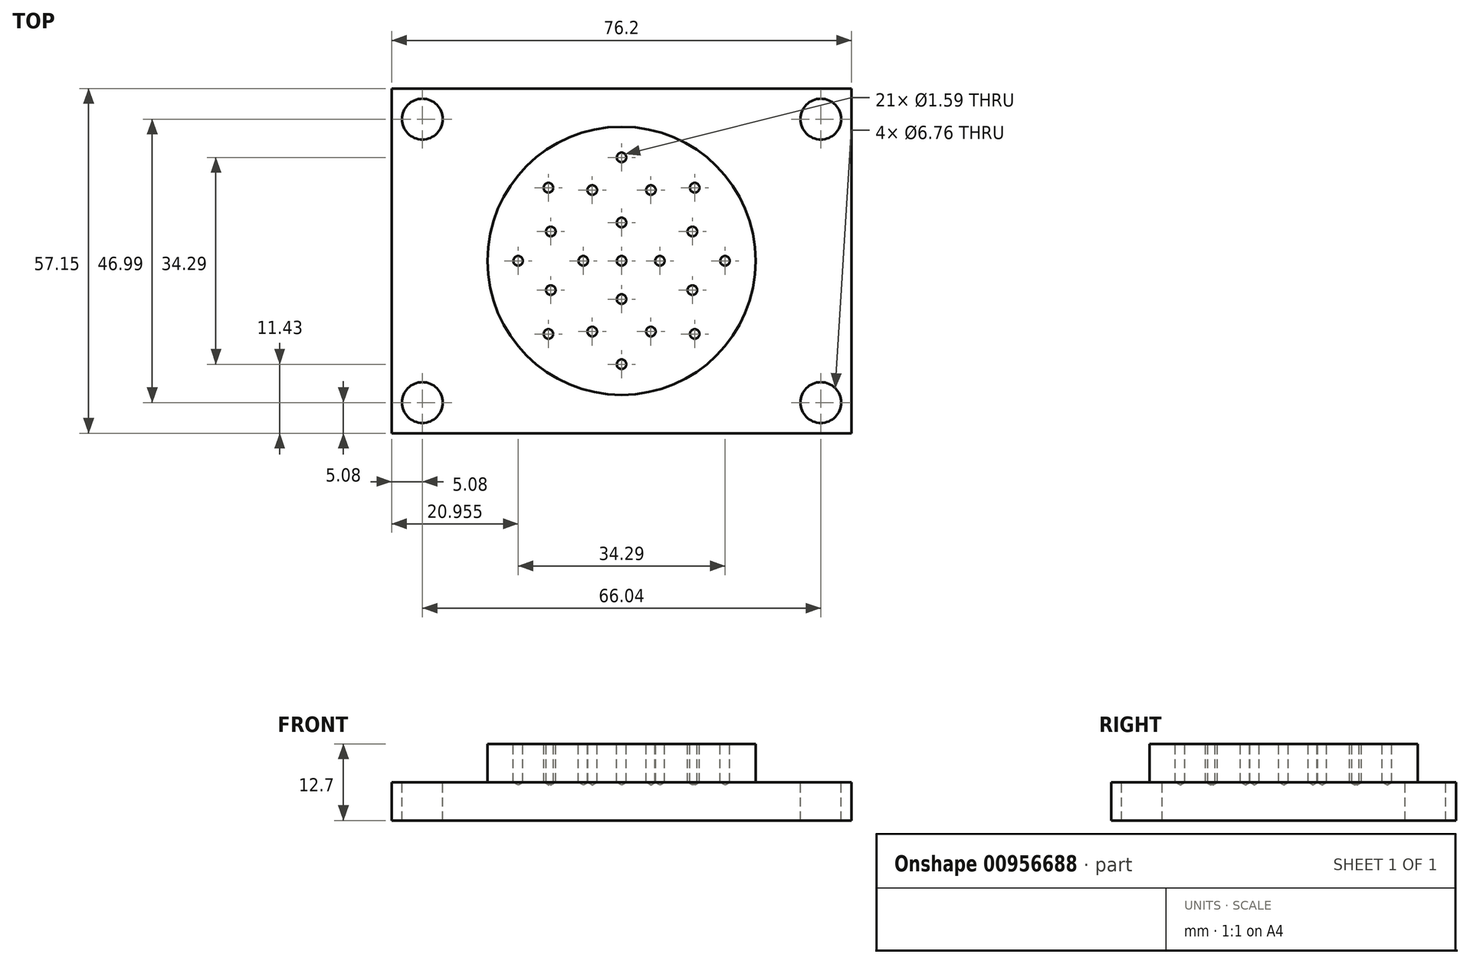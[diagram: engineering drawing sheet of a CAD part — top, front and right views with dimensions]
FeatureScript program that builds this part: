
annotation { "Feature Type Name" : "Feature", "Feature Type Description" : "" }
export const myFeature = defineFeature(function(context is Context, id is Id, definition is map)
    precondition{}
    {
        {
            var Q0;
            Q0=qCreatedBy(makeId("Top.planeOp"),FACE);
            var sketch = newSketch(context, id + "F0", { "sketchPlane" : qUnion([Q0])});
            skLineSegment(sketch, "E0.bottom", {"start": v(0, 0) * mm, "end": v(76.2, 0) * mm});
            skLineSegment(sketch, "E0.top", {"start": v(0, 57.15) * mm, "end": v(76.2, 57.15) * mm});
            skLineSegment(sketch, "E0.left", {"start": v(0, 0) * mm, "end": v(0, 57.15) * mm});
            skLineSegment(sketch, "E0.right", {"start": v(76.2, 0) * mm, "end": v(76.2, 57.15) * mm});
            skSolve(sketch);
        }
        {
            var Q0;
            Q0=makeQuery(id+"F0.imprint","IMPRINT",FACE,{"disambiguationData":[TD([[makeQuery(id+"F0.imprint","IMPRINT",EDGE,{"derivedFrom":sQuery(id+"F0.wireOp",EDGE,"E0.bottom")}),1.0]])]});
            extrude(context, id + "F1", {"entities" : qUnion([Q0]), "depth" : 6.35 * mm, "offsetDistance" : 25.4 * mm});
        }
        {
            var Q0;
            Q0=makeQuery(id+"F1.opExtrude","CAP_FACE",FACE,{"disambiguationData":[OSD([sQuery(id+"F0.wireOp",EDGE,"E0.bottom"),sQuery(id+"F0.wireOp",EDGE,"E0.top"),sQuery(id+"F0.wireOp",EDGE,"E0.left"),sQuery(id+"F0.wireOp",EDGE,"E0.right")])],"isStart":false});
            var sketch = newSketch(context, id + "F2", { "sketchPlane" : qUnion([Q0])});
            skCircle(sketch, "E1", {"center": v(38.1, 28.57) * mm, "radius": 22.23 * mm});
            skLineSegment(sketch, "E2", {"start": v(0, 0) * mm, "end": v(76.2, 57.15) * mm, "construction": true});
            skSolve(sketch);
        }
        {
            var Q0;
            Q0=makeQuery(id+"F2.imprint","IMPRINT",FACE,{"disambiguationData":[TD([[makeQuery(id+"F2.imprint","IMPRINT",EDGE,{"derivedFrom":sQuery(id+"F2.wireOp",EDGE,"E1")}),1.0]])]});
            extrude(context, id + "F3", {"entities" : qUnion([Q0]), "operationType" : NewBodyOperationType.ADD, "depth" : 6.35 * mm, "offsetDistance" : 25.4 * mm});
        }
        {
            var Q0;
            Q0=makeQuery(id+"F1.opExtrude","CAP_FACE",FACE,{"disambiguationData":[OSD([sQuery(id+"F0.wireOp",EDGE,"E0.bottom"),sQuery(id+"F0.wireOp",EDGE,"E0.top"),sQuery(id+"F0.wireOp",EDGE,"E0.left"),sQuery(id+"F0.wireOp",EDGE,"E0.right")])],"isStart":false});
            var sketch = newSketch(context, id + "F4", { "sketchPlane" : qUnion([Q0])});
            skPoint(sketch, "E3", {"position": v(5.08, 5.08) * mm});
            skLineSegment(sketch, "E4.bottom", {"start": v(5.08, 5.08) * mm, "end": v(71.12, 5.08) * mm, "construction": true});
            skLineSegment(sketch, "E4.top", {"start": v(5.08, 52.07) * mm, "end": v(71.12, 52.07) * mm, "construction": true});
            skLineSegment(sketch, "E4.left", {"start": v(5.08, 5.08) * mm, "end": v(5.08, 52.07) * mm, "construction": true});
            skLineSegment(sketch, "E4.right", {"start": v(71.12, 5.08) * mm, "end": v(71.12, 52.07) * mm, "construction": true});
            skSolve(sketch);
        }
        {
            var Q0;
            Q0=sQuery(id+"F4.wireOp",VERTEX,"E3");
            var Q1;
            Q1=sQuery(id+"F4.wireOp",VERTEX,"E4.top.start");
            var Q2;
            Q2=sQuery(id+"F4.wireOp",VERTEX,"E4.top.end");
            var Q3;
            Q3=sQuery(id+"F4.wireOp",VERTEX,"E4.bottom.end");
            var Q4;
            Q4=makeQuery(id+"F1.opExtrude","SWEPT_BODY",BODY,{"disambiguationData":[OSD([sQuery(id+"F0.wireOp",EDGE,"E0.bottom"),sQuery(id+"F0.wireOp",EDGE,"E0.top"),sQuery(id+"F0.wireOp",EDGE,"E0.left"),sQuery(id+"F0.wireOp",EDGE,"E0.right")])]});
            hole(context, id + "F5", {"style" : HoleStyle.SIMPLE, "endStyle" : HoleEndStyle.THROUGH, "standardTappedOrClearance" : lookupTablePath({ "fit" : "Close (ASME)", "standard" : "ANSI", "size" : "1/4", "type" : "Clearance" }), "standardBlindInLast" : lookupTablePath({ "fit" : "Close", "standard" : "ANSI", "engagement" : "75%", "pitch" : "20 tpi", "size" : "1/4", "type" : "Clearance & tapped" }), "holeDiameter" : 6.76 * mm, "majorDiameter" : 6.35 * mm, "isTappedThrough" : true, "tappedDepth" : 12.7 * mm, "tapClearance" : 3, "startFromSketch" : true, "locations" : qUnion([Q0, Q1, Q2, Q3]), "scope" : qUnion([Q4])});
        }
        {
            var Q0;
            Q0=makeQuery(id+"F3.opExtrude","CAP_FACE",FACE,{"disambiguationData":[OSD([sQuery(id+"F2.wireOp",EDGE,"E1")])],"isStart":false});
            var sketch = newSketch(context, id + "F6", { "sketchPlane" : qUnion([Q0])});
            skCircle(sketch, "E5.0", {"center": v(38.1, 28.57) * mm, "radius": 22.23 * mm});
            skPoint(sketch, "E6", {"position": v(38.1, 34.92) * mm});
            skPoint(sketch, "E7", {"position": v(33.24, 40.3) * mm});
            skPoint(sketch, "E8", {"position": v(38.1, 45.72) * mm});
            skLineSegment(sketch, "E9", {"start": v(38.1, 45.72) * mm, "end": v(38.1, 28.57) * mm, "construction": true});
            skLineSegment(sketch, "E10", {"start": v(38.1, 28.57) * mm, "end": v(33.24, 40.3) * mm, "construction": true});
            skPoint(sketch, "E11.1.0", {"position": v(25.98, 40.7) * mm});
            skPoint(sketch, "E11.2.0", {"position": v(20.95, 28.57) * mm});
            skPoint(sketch, "E11.3.0", {"position": v(25.98, 16.45) * mm});
            skPoint(sketch, "E11.4.0", {"position": v(38.1, 11.43) * mm});
            skPoint(sketch, "E11.5.0", {"position": v(50.22, 16.45) * mm});
            skPoint(sketch, "E11.6.0", {"position": v(55.24, 28.57) * mm});
            skPoint(sketch, "E11.7.0", {"position": v(50.22, 40.7) * mm});
            skPoint(sketch, "E12.1.0", {"position": v(26.37, 33.44) * mm});
            skPoint(sketch, "E12.2.0", {"position": v(26.37, 23.71) * mm});
            skPoint(sketch, "E12.3.0", {"position": v(33.24, 16.84) * mm});
            skPoint(sketch, "E12.4.0", {"position": v(42.96, 16.84) * mm});
            skPoint(sketch, "E12.5.0", {"position": v(49.83, 23.71) * mm});
            skPoint(sketch, "E12.6.0", {"position": v(49.83, 33.44) * mm});
            skPoint(sketch, "E12.7.0", {"position": v(42.96, 40.3) * mm});
            skPoint(sketch, "E13.1.0", {"position": v(31.75, 28.57) * mm});
            skPoint(sketch, "E13.2.0", {"position": v(38.1, 22.22) * mm});
            skPoint(sketch, "E13.3.0", {"position": v(44.45, 28.57) * mm});
            skSolve(sketch);
        }
        {
            var Q0;
            Q0=sQuery(id+"F6.wireOp",VERTEX,"E8");
            var Q1;
            Q1=sQuery(id+"F6.wireOp",VERTEX,"E11.1.0");
            var Q2;
            Q2=sQuery(id+"F6.wireOp",VERTEX,"E11.2.0");
            var Q3;
            Q3=sQuery(id+"F6.wireOp",VERTEX,"E11.3.0");
            var Q4;
            Q4=sQuery(id+"F6.wireOp",VERTEX,"E11.4.0");
            var Q5;
            Q5=sQuery(id+"F6.wireOp",VERTEX,"E11.5.0");
            var Q6;
            Q6=sQuery(id+"F6.wireOp",VERTEX,"E11.6.0");
            var Q7;
            Q7=sQuery(id+"F6.wireOp",VERTEX,"E11.7.0");
            var Q8;
            Q8=sQuery(id+"F6.wireOp",VERTEX,"E12.7.0");
            var Q9;
            Q9=sQuery(id+"F6.wireOp",VERTEX,"E7");
            var Q10;
            Q10=sQuery(id+"F6.wireOp",VERTEX,"E12.1.0");
            var Q11;
            Q11=sQuery(id+"F6.wireOp",VERTEX,"E12.2.0");
            var Q12;
            Q12=sQuery(id+"F6.wireOp",VERTEX,"E12.3.0");
            var Q13;
            Q13=sQuery(id+"F6.wireOp",VERTEX,"E12.4.0");
            var Q14;
            Q14=sQuery(id+"F6.wireOp",VERTEX,"E12.5.0");
            var Q15;
            Q15=sQuery(id+"F6.wireOp",VERTEX,"E12.6.0");
            var Q16;
            Q16=sQuery(id+"F6.wireOp",VERTEX,"E6");
            var Q17;
            Q17=sQuery(id+"F6.wireOp",VERTEX,"E13.1.0");
            var Q18;
            Q18=sQuery(id+"F6.wireOp",VERTEX,"E13.2.0");
            var Q19;
            Q19=sQuery(id+"F6.wireOp",VERTEX,"E13.3.0");
            var Q20;
            Q20=sQuery(id+"F6.wireOp",VERTEX,"E5.0.center");
            var Q21;
            Q21=makeQuery(id+"F1.opExtrude","SWEPT_BODY",BODY,{"disambiguationData":[OSD([sQuery(id+"F0.wireOp",EDGE,"E0.bottom"),sQuery(id+"F0.wireOp",EDGE,"E0.top"),sQuery(id+"F0.wireOp",EDGE,"E0.left"),sQuery(id+"F0.wireOp",EDGE,"E0.right")])]});
            hole(context, id + "F7", {"style" : HoleStyle.SIMPLE, "endStyle" : HoleEndStyle.BLIND, "holeDiameter" : 1.59 * mm, "majorDiameter" : 6.35 * mm, "holeDepth" : 6.35 * mm, "isTappedThrough" : true, "tappedDepth" : 12.7 * mm, "tapClearance" : 3, "locations" : qUnion([Q0, Q1, Q2, Q3, Q4, Q5, Q6, Q7, Q8, Q9, Q10, Q11, Q12, Q13, Q14, Q15, Q16, Q17, Q18, Q19, Q20]), "scope" : qUnion([Q21])});
        }
    });
